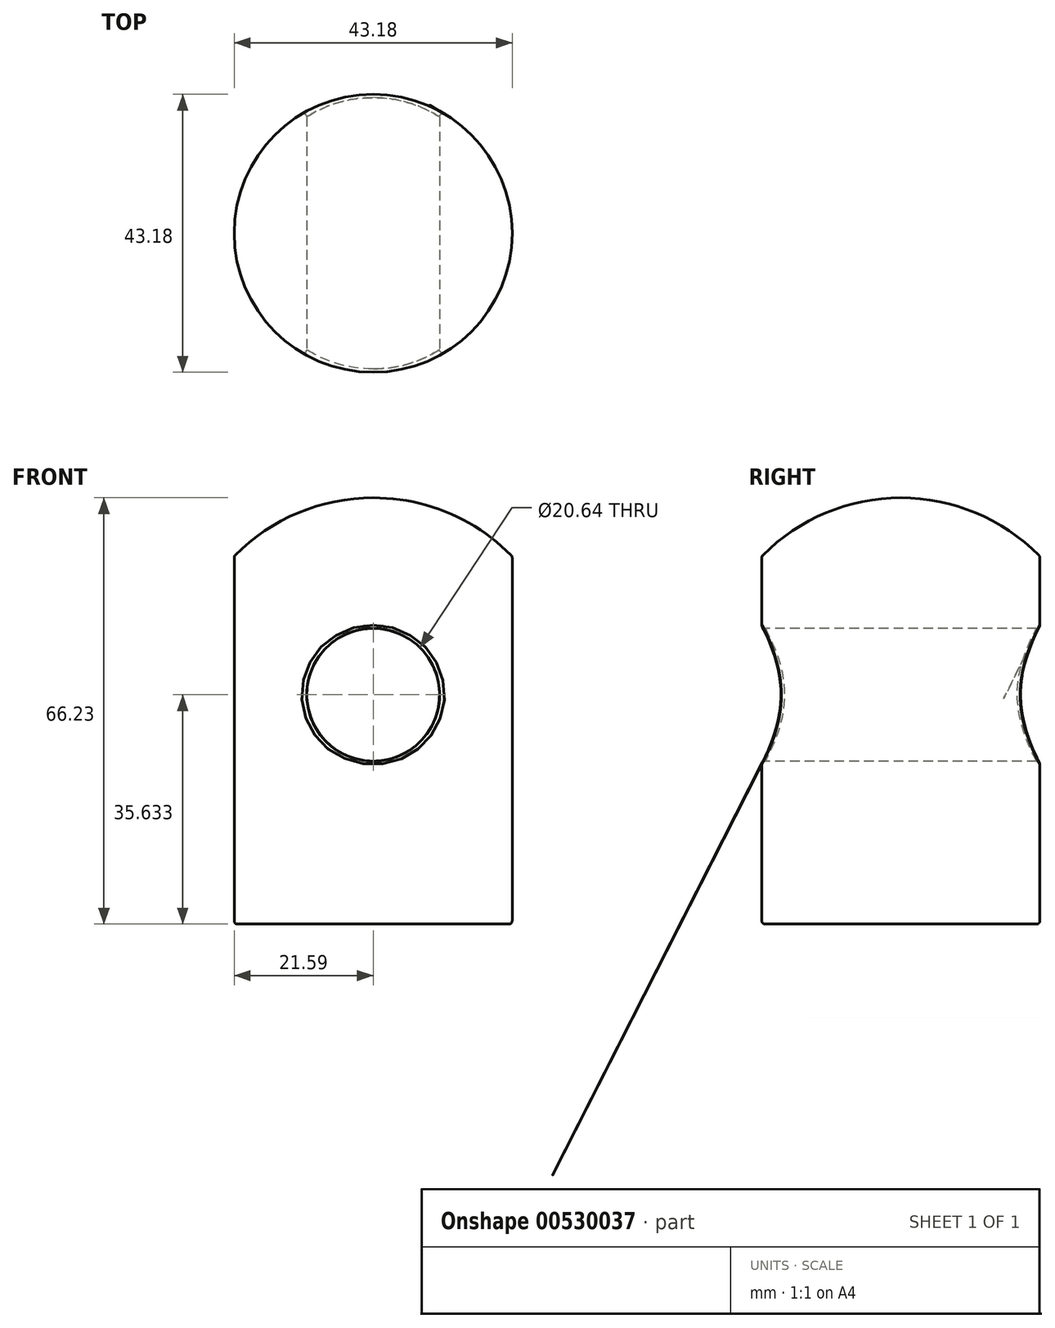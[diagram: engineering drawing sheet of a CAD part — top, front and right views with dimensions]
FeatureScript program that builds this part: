
annotation { "Feature Type Name" : "Feature", "Feature Type Description" : "" }
export const myFeature = defineFeature(function(context is Context, id is Id, definition is map)
    precondition{}
    {
        {
            var Q0;
            Q0=qCreatedBy(makeId("Front.planeOp"),FACE);
            var sketch = newSketch(context, id + "F0", { "sketchPlane" : qUnion([Q0])});
            skLineSegment(sketch, "E0", {"start": v(0, 10.87) * mm, "end": v(0, -55.42) * mm});
            skLineSegment(sketch, "E1", {"start": v(0, -55.42) * mm, "end": v(-21.59, -55.42) * mm});
            skLineSegment(sketch, "E2", {"start": v(-21.59, -55.42) * mm, "end": v(-21.59, 1.73) * mm});
            skArc(sketch, "E3", {"start": v(-21.59, 1.73) * mm, "mid": v(-11.71, 8.45) * mm, "end": v(0, 10.81) * mm});
            skPoint(sketch, "E4", {"position": v(0, -22.27) * mm});
            skSolve(sketch);
        }
        {
            var Q0;
            Q0=qCreatedBy(makeId("Front.planeOp"),FACE);
            var sketch = newSketch(context, id + "F1", { "sketchPlane" : qUnion([Q0])});
            skCircle(sketch, "E5", {"center": v(0, -19.79) * mm, "radius": 10.32 * mm});
            skSolve(sketch);
        }
        {
            var Q0;
            Q0=qSketchRegion(id+"F0",true);
            var Q1;
            Q1=sQuery(id+"F0.wireOp",EDGE,"E0");
            revolve(context, id + "F2", {"entities" : qUnion([Q0]), "axis" : qUnion([Q1]), "revolveType" : RevolveType.FULL});
        }
        {
            var Q0;
            Q0=qSketchRegion(id+"F1",true);
            extrude(context, id + "F3", {"entities" : qUnion([Q0]), "operationType" : NewBodyOperationType.REMOVE, "endBound" : BoundingType.THROUGH_ALL, "oppositeDirection" : true, "depth" : 25.4 * mm});
        }
        {
            var Q0;
            Q0=qSketchRegion(id+"F1",true);
            extrude(context, id + "F4", {"entities" : qUnion([Q0]), "operationType" : NewBodyOperationType.REMOVE, "endBound" : BoundingType.THROUGH_ALL, "depth" : 25.4 * mm});
        }
        {
            var Q0;
            Q0=makeQuery(id+"F2.opRevolve","SWEPT_EDGE",EDGE,{"disambiguationData":[OSD([sQuery(id+"F0.wireOp",EDGE,"E2"),sQuery(id+"F0.wireOp",EDGE,"E3")])]});
            var Q1;
            Q1=makeQuery(id+"F4.boolean.opBoolean","INTERSECT",EDGE,{"derivedFrom":[makeQuery(id+"F2.opRevolve","SWEPT_FACE",FACE,{"disambiguationData":[OSD([sQuery(id+"F0.wireOp",EDGE,"E2")])]}),makeQuery(id+"F4.opExtrude","SWEPT_FACE",FACE,{"disambiguationData":[OSD([sQuery(id+"F1.wireOp",EDGE,"E5")])]})]});
            var Q2;
            Q2=makeQuery(id+"F2.opRevolve","SWEPT_EDGE",EDGE,{"disambiguationData":[OSD([sQuery(id+"F0.wireOp",EDGE,"E1"),sQuery(id+"F0.wireOp",EDGE,"E2")])]});
            var Q3;
            Q3=makeQuery(id+"F3.boolean.opBoolean","INTERSECT",EDGE,{"derivedFrom":[makeQuery(id+"F2.opRevolve","SWEPT_FACE",FACE,{"disambiguationData":[OSD([sQuery(id+"F0.wireOp",EDGE,"E2")])]}),makeQuery(id+"F3.opExtrude","SWEPT_FACE",FACE,{"disambiguationData":[OSD([sQuery(id+"F1.wireOp",EDGE,"E5")])]})]});
            fillet(context, id + "F5", {"entities" : qUnion([Q0, Q1, Q2, Q3]), "radius" : 0.5 * mm, "tangentPropagation" : true, "allowEdgeOverflow" : false});
        }
    });
